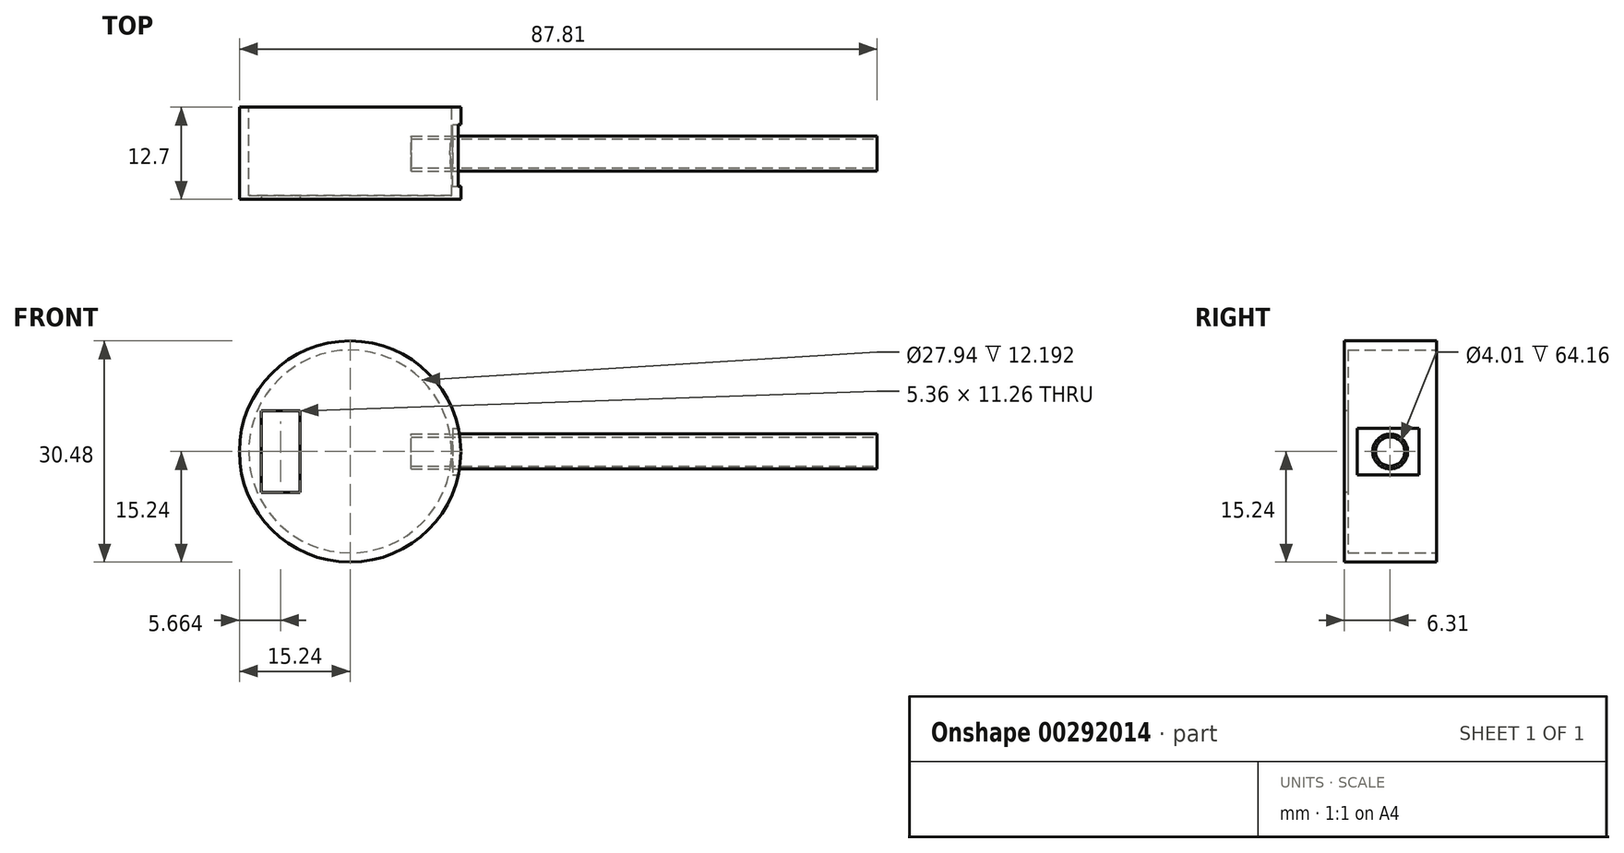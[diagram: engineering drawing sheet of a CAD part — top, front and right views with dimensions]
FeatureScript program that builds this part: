
annotation { "Feature Type Name" : "Feature", "Feature Type Description" : "" }
export const myFeature = defineFeature(function(context is Context, id is Id, definition is map)
    precondition{}
    {
        {
            var Q0;
            Q0=qCreatedBy(makeId("Front.planeOp"),FACE);
            var sketch = newSketch(context, id + "F0", { "sketchPlane" : qUnion([Q0])});
            skCircle(sketch, "E0", {"center": v(0, 0) * mm, "radius": 15.24 * mm});
            skSolve(sketch);
        }
        {
            var Q0;
            Q0=makeQuery(id+"F0.imprint","IMPRINT",FACE,{"disambiguationData":[TD([[makeQuery(id+"F0.imprint","IMPRINT",EDGE,{"derivedFrom":sQuery(id+"F0.wireOp",EDGE,"E0")}),1.0]])]});
            extrude(context, id + "F1", {"entities" : qUnion([Q0]), "depth" : 12.7 * mm});
        }
        {
            var Q0;
            Q0=makeQuery(id+"F1.opExtrude","CAP_FACE",FACE,{"disambiguationData":[OSD([sQuery(id+"F0.wireOp",EDGE,"E0")])],"isStart":true});
            var sketch = newSketch(context, id + "F2", { "sketchPlane" : qUnion([Q0])});
            skCircle(sketch, "E1", {"center": v(0, 0) * mm, "radius": 13.97 * mm});
            skSolve(sketch);
        }
        {
            var Q0;
            Q0=makeQuery(id+"F2.imprint","IMPRINT",FACE,{"disambiguationData":[TD([[makeQuery(id+"F2.imprint","IMPRINT",EDGE,{"derivedFrom":sQuery(id+"F2.wireOp",EDGE,"E1")}),1.0]])]});
            extrude(context, id + "F3", {"entities" : qUnion([Q0]), "operationType" : NewBodyOperationType.REMOVE, "oppositeDirection" : true, "depth" : 12.2 * mm});
        }
        {
            var Q0;
            Q0=qCreatedBy(makeId("Right.planeOp"),FACE);
            cPlane(context, id + "F4", {"entities" : qUnion([Q0]), "cplaneType" : CPlaneType.OFFSET, "offset" : 31.75 * mm, "width" : 152.4 * mm, "height" : 152.4 * mm});
        }
        {
            var Q0;
            Q0=qCreatedBy(id+"F4.planeOp",FACE);
            var sketch = newSketch(context, id + "F5", { "sketchPlane" : qUnion([Q0])});
            skLineSegment(sketch, "E2.bottom", {"start": v(-10.91, 3.2) * mm, "end": v(-2.42, 3.2) * mm});
            skLineSegment(sketch, "E2.top", {"start": v(-10.91, -3.2) * mm, "end": v(-2.42, -3.2) * mm});
            skLineSegment(sketch, "E2.left", {"start": v(-10.91, 3.2) * mm, "end": v(-10.91, -3.2) * mm});
            skLineSegment(sketch, "E2.right", {"start": v(-2.42, 3.2) * mm, "end": v(-2.42, -3.2) * mm});
            skPoint(sketch, "E2.middle", {"position": v(-6.67, 0) * mm});
            skSolve(sketch);
        }
        {
            var Q0;
            Q0=makeQuery(id+"F5.imprint","IMPRINT",FACE,{"disambiguationData":[TD([[makeQuery(id+"F5.imprint","IMPRINT",EDGE,{"derivedFrom":sQuery(id+"F5.wireOp",EDGE,"E2.bottom")}),-1.0]])]});
            extrude(context, id + "F6", {"entities" : qUnion([Q0]), "operationType" : NewBodyOperationType.REMOVE, "oppositeDirection" : true, "depth" : 17.63 * mm});
        }
        {
            var Q0;
            Q0=qCreatedBy(id+"F4.planeOp",FACE);
            var sketch = newSketch(context, id + "F7", { "sketchPlane" : qUnion([Q0])});
            skCircle(sketch, "E3", {"center": v(-6.39, 0) * mm, "radius": 2.4 * mm});
            skSolve(sketch);
        }
        {
            var Q0;
            Q0=makeQuery(id+"F7.imprint","IMPRINT",FACE,{"disambiguationData":[TD([[makeQuery(id+"F7.imprint","IMPRINT",EDGE,{"derivedFrom":sQuery(id+"F7.wireOp",EDGE,"E3")}),1.0]])]});
            extrude(context, id + "F8", {"entities" : qUnion([Q0]), "operationType" : NewBodyOperationType.ADD, "oppositeDirection" : true, "depth" : 23.34 * mm});
        }
        {
            var Q0;
            Q0=makeQuery(id+"F8.opExtrude","CAP_FACE",FACE,{"disambiguationData":[OSD([sQuery(id+"F7.wireOp",EDGE,"E3")])],"isStart":true});
            extrude(context, id + "F9", {"entities" : qUnion([Q0]), "operationType" : NewBodyOperationType.ADD, "depth" : 18.8 * mm});
        }
        {
            var Q0;
            Q0=makeQuery(id+"F9.opExtrude","CAP_FACE",FACE,{"disambiguationData":[OSD([sQuery(id+"F7.wireOp",EDGE,"E3")])],"isStart":false});
            var sketch = newSketch(context, id + "F10", { "sketchPlane" : qUnion([Q0])});
            skCircle(sketch, "E4", {"center": v(-6.39, 0) * mm, "radius": 2 * mm});
            skSolve(sketch);
        }
        {
            var Q0;
            Q0=makeQuery(id+"F10.imprint","IMPRINT",FACE,{"disambiguationData":[TD([[makeQuery(id+"F10.imprint","IMPRINT",EDGE,{"derivedFrom":sQuery(id+"F10.wireOp",EDGE,"E4")}),1.0]])]});
            extrude(context, id + "F11", {"entities" : qUnion([Q0]), "operationType" : NewBodyOperationType.REMOVE, "oppositeDirection" : true, "depth" : 43.6 * mm});
        }
        {
            var Q0;
            Q0=makeQuery(id+"F9.opExtrude","CAP_FACE",FACE,{"disambiguationData":[OSD([sQuery(id+"F7.wireOp",EDGE,"E3")])],"isStart":false});
            var sketch = newSketch(context, id + "F12", { "sketchPlane" : qUnion([Q0])});
            skSolve(sketch);
        }
        {
            var Q0;
            Q0=makeQuery(id+"F12.imprint","IMPRINT",FACE,{"disambiguationData":[TD([[makeQuery(id+"F12.imprint","IMPRINT",EDGE,{"derivedFrom":makeQuery(id+"F9.opExtrude","CAP_EDGE",EDGE,{"disambiguationData":[OSD([sQuery(id+"F7.wireOp",EDGE,"E3")])],"isStart":false})}),1.0]])]});
            extrude(context, id + "F13", {"entities" : qUnion([Q0]), "operationType" : NewBodyOperationType.ADD, "depth" : 25.4 * mm});
        }
        {
            var Q0;
            Q0=makeQuery(id+"F13.opExtrude","CAP_FACE",FACE,{"disambiguationData":[OSD([sQuery(id+"F7.wireOp",EDGE,"E3"),sQuery(id+"F10.wireOp",EDGE,"E4")])],"isStart":false});
            extrude(context, id + "F14", {"entities" : qUnion([Q0]), "operationType" : NewBodyOperationType.REMOVE, "oppositeDirection" : true, "depth" : 16.15 * mm});
        }
        {
            var Q0;
            Q0=makeQuery(id+"F14.boolean.opBoolean","COPY",FACE,{"derivedFrom":makeQuery(id+"F14.opExtrude","CAP_FACE",FACE,{"disambiguationData":[OSD([sQuery(id+"F7.wireOp",EDGE,"E3"),sQuery(id+"F10.wireOp",EDGE,"E4")])],"isStart":false})});
            extrude(context, id + "F15", {"entities" : qUnion([Q0]), "operationType" : NewBodyOperationType.ADD, "depth" : 12.78 * mm});
        }
        {
            var Q0;
            Q0=makeQuery(id+"F1.opExtrude","CAP_FACE",FACE,{"disambiguationData":[OSD([sQuery(id+"F0.wireOp",EDGE,"E0")])],"isStart":false});
            var sketch = newSketch(context, id + "F16", { "sketchPlane" : qUnion([Q0])});
            skLineSegment(sketch, "E5.bottom", {"start": v(-6.9, -5.63) * mm, "end": v(-12.26, -5.63) * mm});
            skLineSegment(sketch, "E5.top", {"start": v(-6.9, 5.63) * mm, "end": v(-12.26, 5.63) * mm});
            skLineSegment(sketch, "E5.left", {"start": v(-6.9, -5.63) * mm, "end": v(-6.9, 5.63) * mm});
            skLineSegment(sketch, "E5.right", {"start": v(-12.26, -5.63) * mm, "end": v(-12.26, 5.63) * mm});
            skPoint(sketch, "E5.middle", {"position": v(-9.58, 0) * mm});
            skSolve(sketch);
        }
        {
            var Q0;
            Q0=makeQuery(id+"F16.imprint","IMPRINT",FACE,{"disambiguationData":[TD([[makeQuery(id+"F16.imprint","IMPRINT",EDGE,{"derivedFrom":sQuery(id+"F16.wireOp",EDGE,"E5.bottom")}),-1.0]])]});
            extrude(context, id + "F17", {"entities" : qUnion([Q0]), "operationType" : NewBodyOperationType.REMOVE, "oppositeDirection" : true, "depth" : 25.4 * mm});
        }
    });
